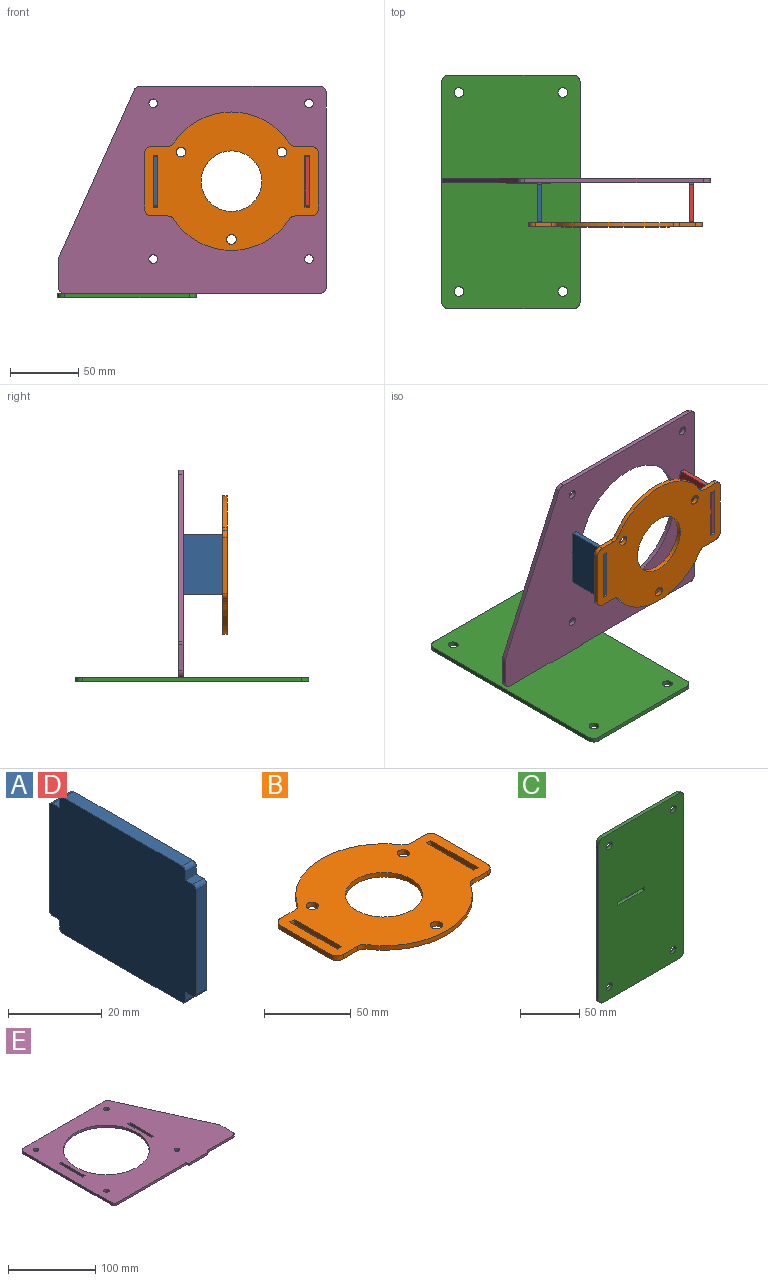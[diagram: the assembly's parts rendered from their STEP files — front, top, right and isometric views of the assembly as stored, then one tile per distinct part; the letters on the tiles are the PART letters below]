
ASSEMBLY  parts=5 mates=4
PART A: 22 faces, bbox 3.2x44.2x35.6 mm
  f0: plane 3.18x2.16mm, normal (0,-1,0), area 6.9mm2, adj f1,f12,f13,f15
  f1: plane 3.18x2.16mm, normal (0,0,-1), area 6.9mm2, adj f0,f12,f13,f16
  f2: plane 27.18x3.18mm, normal (0,-1,0), area 86.3mm2, adj f12,f13,f16,f17
  f3: plane 3.18x2.16mm, normal (0,0,1), area 6.9mm2, adj f4,f12,f13,f17
  f4: plane 3.18x2.16mm, normal (0,-1,0), area 6.9mm2, adj f3,f12,f13,f18
  f5: plane 35.81x3.18mm, normal (0,0,1), area 113.7mm2, adj f12,f13,f18,f19
  f6: plane 3.18x2.16mm, normal (0,1,0), area 6.9mm2, adj f7,f12,f13,f19
  f7: plane 3.18x2.16mm, normal (0,0,1), area 6.9mm2, adj f6,f12,f13,f20
  f8: plane 27.18x3.18mm, normal (0,1,0), area 86.3mm2, adj f12,f13,f20,f21
  f9: plane 3.18x2.16mm, normal (0,0,-1), area 6.9mm2, adj f10,f12,f13,f21
  f10: plane 3.18x2.16mm, normal (0,1,0), area 6.9mm2, adj f9,f12,f13,f14
  f11: plane 35.81x3.18mm, normal (0,0,-1), area 113.7mm2, adj f12,f13,f14,f15
  f12: plane 44.2x35.56mm, normal (-1,0,0), area 1529.5mm2, adj f0,f1,f2,f3,f4,f5,f6,f7
  f13: plane 44.2x35.56mm, normal (1,0,0), area 1529.5mm2, adj f0,f1,f2,f3,f4,f5,f6,f7
  f14: cylinder r=1.02mm len=3.18mm, axis (1,0,0), area 5.1mm2, adj f10,f11,f12,f13
  f15: cylinder r=1.02mm len=3.18mm, axis (1,0,0), area 5.1mm2, adj f0,f11,f12,f13
  f16: cylinder r=1.02mm len=3.18mm, axis (1,0,0), area 5.1mm2, adj f1,f2,f12,f13
  f17: cylinder r=1.02mm len=3.18mm, axis (-1,0,0), area 5.1mm2, adj f2,f3,f12,f13
  f18: cylinder r=1.02mm len=3.18mm, axis (1,0,0), area 5.1mm2, adj f4,f5,f12,f13
  f19: cylinder r=1.02mm len=3.18mm, axis (1,0,0), area 5.1mm2, adj f5,f6,f12,f13
  f20: cylinder r=1.02mm len=3.18mm, axis (1,0,0), area 5.1mm2, adj f7,f8,f12,f13
  f21: cylinder r=1.02mm len=3.18mm, axis (-1,0,0), area 5.1mm2, adj f8,f9,f12,f13
PART B: 30 faces, bbox 127.5x101.6x3.2 mm
  f0: plane 38.35x3.18mm, normal (-1,0,0), area 121.8mm2, adj f1,f19,f20,f21
  f1: plane 3.43x3.18mm, normal (0,1,0), area 10.9mm2, adj f0,f2,f20,f21
  f2: plane 38.35x3.18mm, normal (1,0,0), area 121.8mm2, adj f1,f19,f20,f21
  f3: plane 11.92x3.18mm, normal (0,1,0), area 37.9mm2, adj f20,f21,f22,f29
  f4: cylinder r=50.8mm len=85mm, axis (0,0,-1), area 319.7mm2, adj f20,f21,f22,f23
  f5: plane 11.92x3.18mm, normal (0,1,0), area 37.9mm2, adj f20,f21,f23,f24
  f6: plane 40.89x3.18mm, normal (-1,0,0), area 129.8mm2, adj f20,f21,f24,f25
  f7: plane 11.92x3.18mm, normal (0,-1,0), area 37.9mm2, adj f20,f21,f25,f26
  f8: cylinder r=50.8mm len=85mm, axis (0,0,-1), area 319.7mm2, adj f20,f21,f26,f27
  f9: plane 11.92x3.18mm, normal (0,-1,0), area 37.9mm2, adj f20,f21,f27,f28
  f10: plane 3.43x3.18mm, normal (0,1,0), area 10.9mm2, adj f11,f14,f20,f21
  f11: plane 38.35x3.18mm, normal (1,0,0), area 121.8mm2, adj f10,f12,f20,f21
  f12: plane 3.43x3.18mm, normal (0,-1,0), area 10.9mm2, adj f11,f14,f20,f21
  f13: plane 40.89x3.18mm, normal (1,0,0), area 129.8mm2, adj f20,f21,f28,f29
  f14: plane 38.35x3.18mm, normal (-1,0,0), area 121.8mm2, adj f10,f12,f20,f21
  f15: cylinder r=3.57mm len=7.14mm, axis (0,0,-1), area 71.3mm2, adj f20,f21
  f16: cylinder r=3.57mm len=7.14mm, axis (0,0,-1), area 71.3mm2, adj f20,f21
  f17: cylinder r=3.57mm len=7.14mm, axis (0,0,-1), area 71.3mm2, adj f20,f21
  f18: cylinder r=22.23mm len=44.45mm, axis (0,0,-1), area 443.4mm2, adj f20,f21
  f19: plane 3.43x3.18mm, normal (0,-1,0), area 10.9mm2, adj f0,f2,f20,f21
  f20: plane 127.51x101.6mm, normal (0,0,1), area 7705.1mm2, adj f0,f1,f2,f3,f4,f5,f6,f7
  f21: plane 127.51x101.6mm, normal (0,0,-1), area 7705.1mm2, adj f0,f1,f2,f3,f4,f5,f6,f7
  f22: cylinder r=5.08mm len=4.25mm, axis (0,0,-1), area 16mm2, adj f3,f4,f20,f21
  f23: cylinder r=5.08mm len=4.25mm, axis (0,0,-1), area 16mm2, adj f4,f5,f20,f21
  f24: cylinder r=5.08mm len=5.08mm, axis (0,0,-1), area 25.3mm2, adj f5,f6,f20,f21
  f25: cylinder r=5.08mm len=5.08mm, axis (0,0,1), area 25.3mm2, adj f6,f7,f20,f21
  f26: cylinder r=5.08mm len=4.25mm, axis (0,0,-1), area 16mm2, adj f7,f8,f20,f21
  f27: cylinder r=5.08mm len=4.25mm, axis (0,0,-1), area 16mm2, adj f8,f9,f20,f21
  f28: cylinder r=5.08mm len=5.08mm, axis (0,0,-1), area 25.3mm2, adj f9,f13,f20,f21
  f29: cylinder r=5.08mm len=5.08mm, axis (0,0,1), area 25.3mm2, adj f3,f13,f20,f21
PART C: 18 faces, bbox 101.6x3.2x171.5 mm
  f0: plane 91.44x3.18mm, normal (0,0,-1), area 290.3mm2, adj f12,f13,f16,f17
  f1: plane 161.29x3.18mm, normal (1,0,0), area 512.1mm2, adj f12,f13,f14,f17
  f2: plane 91.44x3.18mm, normal (0,0,1), area 290.3mm2, adj f12,f13,f14,f15
  f3: plane 3.68x3.18mm, normal (-1,0,0), area 11.7mm2, adj f4,f10,f12,f13
  f4: plane 32.26x3.18mm, normal (0,0,1), area 102.4mm2, adj f3,f5,f12,f13
  f5: plane 3.68x3.18mm, normal (1,0,0), area 11.7mm2, adj f4,f10,f12,f13
  f6: cylinder r=3.57mm len=7.14mm, axis (0,1,0), area 71.3mm2, adj f12,f13
  f7: cylinder r=3.57mm len=7.14mm, axis (0,1,0), area 71.3mm2, adj f12,f13
  f8: cylinder r=3.57mm len=7.14mm, axis (0,1,0), area 71.3mm2, adj f12,f13
  f9: plane 161.29x3.18mm, normal (-1,0,0), area 512.1mm2, adj f12,f13,f15,f16
  f10: plane 32.26x3.18mm, normal (0,0,-1), area 102.4mm2, adj f3,f5,f12,f13
  f11: cylinder r=3.57mm len=7.14mm, axis (0,1,0), area 71.3mm2, adj f12,f13
  f12: plane 171.45x101.6mm, normal (0,-1,0), area 17118mm2, adj f0,f1,f2,f3,f4,f5,f6,f7
  f13: plane 171.45x101.6mm, normal (0,1,0), area 17118mm2, adj f0,f1,f2,f3,f4,f5,f6,f7
  f14: cylinder r=5.08mm len=5.08mm, axis (0,-1,0), area 25.3mm2, adj f1,f2,f12,f13
  f15: cylinder r=5.08mm len=5.08mm, axis (0,1,0), area 25.3mm2, adj f2,f9,f12,f13
  f16: cylinder r=5.08mm len=5.08mm, axis (0,-1,0), area 25.3mm2, adj f0,f9,f12,f13
  f17: cylinder r=5.08mm len=5.08mm, axis (0,1,0), area 25.3mm2, adj f0,f1,f12,f13
PART D: same geometry as A
PART E: 31 faces, bbox 196.9x155.3x3.2 mm
  f0: plane 3.18x1.91mm, normal (1,0,0), area 6mm2, adj f1,f22,f23,f30
  f1: plane 42.55x3.18mm, normal (0,-1,0), area 135.1mm2, adj f0,f22,f23,f24
  f2: plane 19.23x3.18mm, normal (1,0,0), area 61.1mm2, adj f22,f23,f24,f25
  f3: plane 123.01x55.35mm, normal (0.91,0.41,0), area 428.3mm2, adj f22,f23,f25,f26
  f4: plane 131.34x3.18mm, normal (0,1,0), area 417mm2, adj f22,f23,f26,f27
  f5: plane 142.24x3.18mm, normal (-1,0,0), area 451.6mm2, adj f22,f23,f27,f28
  f6: plane 112.4x3.18mm, normal (0,-1,0), area 356.9mm2, adj f7,f22,f23,f28
  f7: plane 3.18x1.91mm, normal (-1,0,0), area 6mm2, adj f6,f22,f23,f29
  f8: plane 3.68x3.18mm, normal (0,-1,0), area 11.7mm2, adj f9,f14,f22,f23
  f9: plane 38.35x3.18mm, normal (-1,0,0), area 121.8mm2, adj f8,f10,f22,f23
  f10: plane 3.68x3.18mm, normal (0,1,0), area 11.7mm2, adj f9,f14,f22,f23
  f11: plane 3.68x3.18mm, normal (0,-1,0), area 11.7mm2, adj f12,f20,f22,f23
  f12: plane 38.35x3.18mm, normal (-1,0,0), area 121.8mm2, adj f11,f13,f22,f23
  f13: plane 3.68x3.18mm, normal (0,1,0), area 11.7mm2, adj f12,f20,f22,f23
  f14: plane 38.35x3.18mm, normal (1,0,0), area 121.8mm2, adj f8,f10,f22,f23
  f15: cylinder r=49.21mm len=98.43mm, axis (0,0,-1), area 981.7mm2, adj f22,f23
  f16: cylinder r=3.17mm len=6.35mm, axis (0,0,-1), area 63.3mm2, adj f22,f23
  f17: cylinder r=3.17mm len=6.35mm, axis (0,0,-1), area 63.3mm2, adj f22,f23
  f18: cylinder r=3.17mm len=6.35mm, axis (0,0,-1), area 63.3mm2, adj f22,f23
  f19: cylinder r=3.17mm len=6.35mm, axis (0,0,-1), area 63.3mm2, adj f22,f23
  f20: plane 38.35x3.18mm, normal (1,0,0), area 121.8mm2, adj f11,f13,f22,f23
  f21: plane 29.72x3.18mm, normal (0,-1,0), area 94.4mm2, adj f22,f23,f29,f30
  f22: plane 196.85x155.32mm, normal (0,0,1), area 18426.9mm2, adj f0,f1,f2,f3,f4,f5,f6,f7
  f23: plane 196.85x155.32mm, normal (0,0,-1), area 18426.9mm2, adj f0,f1,f2,f3,f4,f5,f6,f7
  f24: cylinder r=5.08mm len=5.08mm, axis (0,0,1), area 25.3mm2, adj f1,f2,f22,f23
  f25: cylinder r=5.08mm len=3.18mm, axis (0,0,-1), area 6.8mm2, adj f2,f3,f22,f23
  f26: cylinder r=5.08mm len=4.63mm, axis (0,0,-1), area 18.5mm2, adj f3,f4,f22,f23
  f27: cylinder r=5.08mm len=5.08mm, axis (0,0,-1), area 25.3mm2, adj f4,f5,f22,f23
  f28: cylinder r=5.08mm len=5.08mm, axis (0,0,1), area 25.3mm2, adj f5,f6,f22,f23
  f29: cylinder r=1.02mm len=3.18mm, axis (0,0,-1), area 5.1mm2, adj f7,f21,f22,f23
  f30: cylinder r=1.02mm len=3.18mm, axis (0,0,1), area 5.1mm2, adj f0,f21,f22,f23
PLACE A rot(axis=(1,0,0),90deg) t=(-273.05,-47.75,92.33)mm
PLACE B rot(axis=(0,0.71,0.71),180deg) t=(-273.05,-51.31,92.08)mm
PLACE C rot(axis=(0,0.71,0.71),180deg) t=(-273.56,-51.56,92.07)mm
PLACE D rot(axis=(1,0,0),90deg) t=(-161.67,-47.75,92.33)mm
PLACE E rot(axis=(0,0.71,0.71),180deg) t=(-273.3,-51.31,92.07)mm
MATE fastened C.f13 <-> E.f6  axis (0,0,1) through (-320.93,-31.75,9.52)mm
MATE fastened E.f23 <-> A.f9  axis (0,-1,0) through (-327.03,-34.92,111.25)mm
MATE fastened A.f7 <-> B.f20  axis (0,-1,0) through (-327.03,-64.13,111.25)mm
MATE fastened D.f7 <-> B.f20  axis (0,-1,0) through (-215.65,-64.13,111.25)mm
